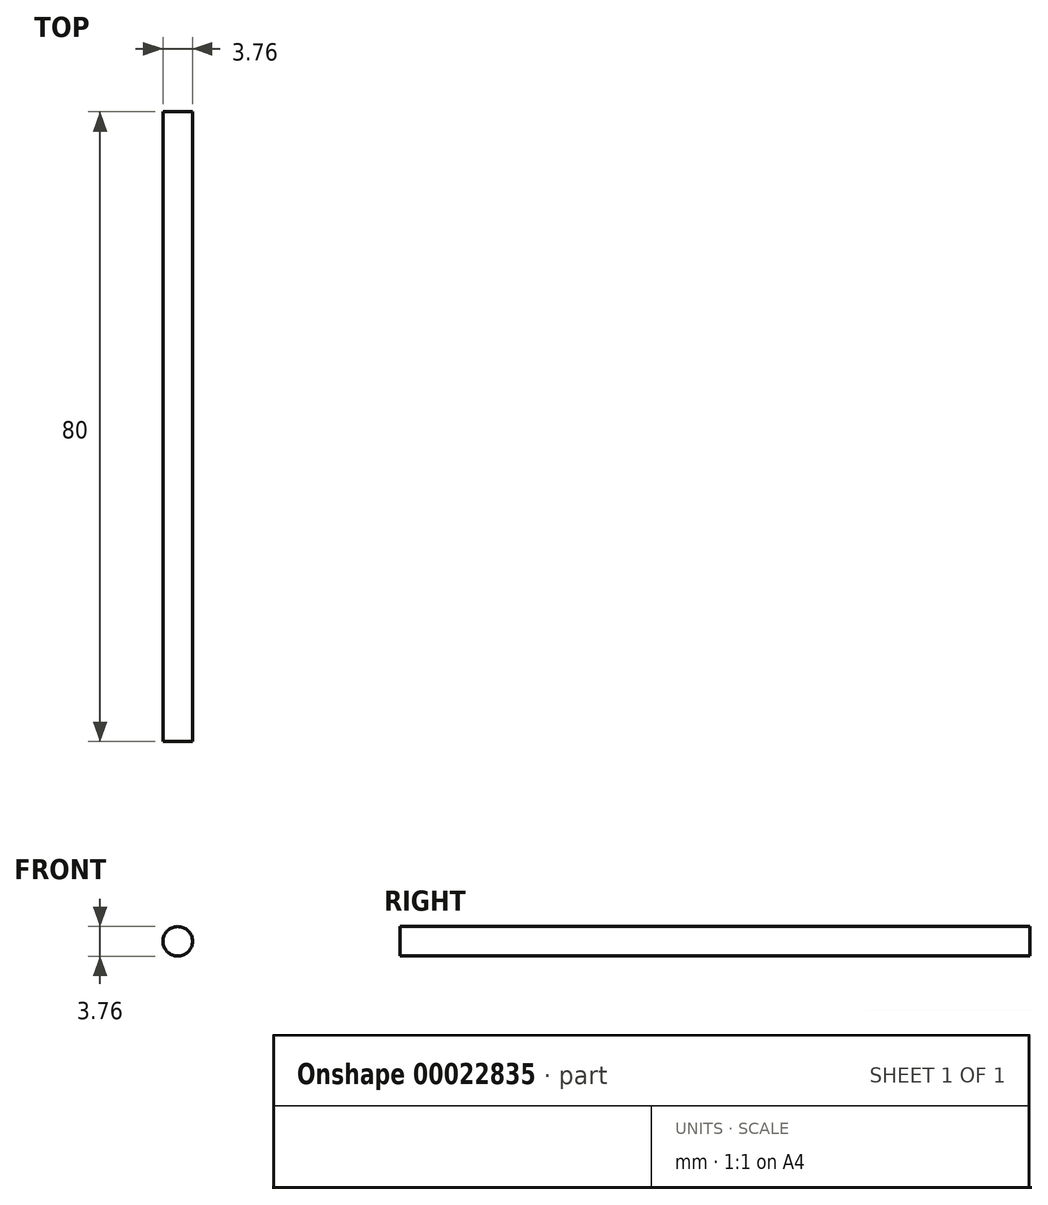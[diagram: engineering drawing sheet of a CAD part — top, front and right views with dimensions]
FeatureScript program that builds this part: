
annotation { "Feature Type Name" : "Feature", "Feature Type Description" : "" }
export const myFeature = defineFeature(function(context is Context, id is Id, definition is map)
    precondition{}
    {
        {
            var Q0;
            Q0=qCreatedBy(makeId("Front.planeOp"),FACE);
            var sketch = newSketch(context, id + "F0", { "sketchPlane" : qUnion([Q0])});
            skCircle(sketch, "E0", {"center": v(0, 0) * mm, "radius": 1.88 * mm});
            skSolve(sketch);
        }
        {
            var Q0;
            Q0=makeQuery(id+"F0.imprint","IMPRINT",FACE,{"disambiguationData":[TD([[makeQuery(id+"F0.imprint","IMPRINT",EDGE,{"derivedFrom":sQuery(id+"F0.wireOp",EDGE,"E0")}),1.0]])]});
            extrude(context, id + "F1", {"entities" : qUnion([Q0]), "oppositeDirection" : true, "depth" : 80 * mm});
        }
    });
